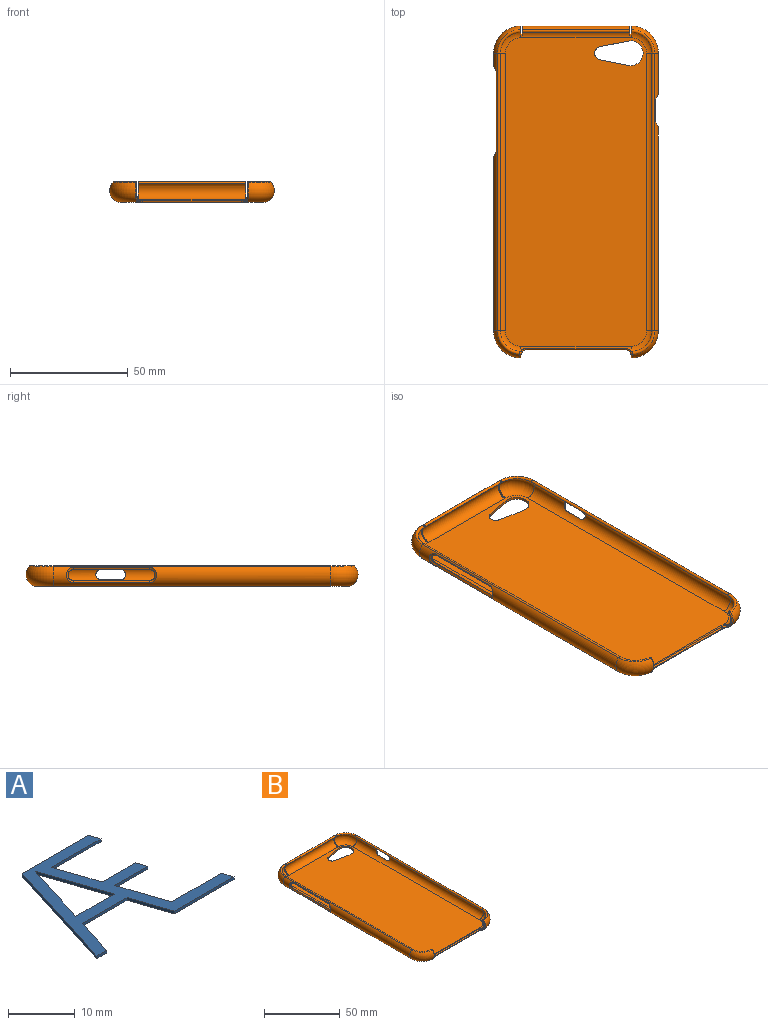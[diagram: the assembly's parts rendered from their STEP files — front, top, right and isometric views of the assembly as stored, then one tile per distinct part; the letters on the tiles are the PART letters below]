
ASSEMBLY  parts=2 mates=1
PART A: 21 faces, bbox 29x23x0.5 mm
  f0: plane 8x2.69mm, normal (0.95,0.32,0), area 4.2mm2, adj f1,f18,f19,f20
  f1: plane 10.46x0.5mm, normal (0,-1,0), area 5.2mm2, adj f0,f2,f19,f20
  f2: plane 2x0.67mm, normal (0.95,0.32,0), area 1.1mm2, adj f1,f3,f19,f20
  f3: plane 14.03x0.5mm, normal (0,1,0), area 7mm2, adj f2,f4,f19,f20
  f4: plane 23x7.2mm, normal (-0.95,0.3,0), area 12.1mm2, adj f3,f5,f19,f20
  f5: plane 2.1x0.5mm, normal (0,-1,0), area 1mm2, adj f4,f6,f19,f20
  f6: plane 7.49x2.35mm, normal (0.95,-0.3,0), area 3.9mm2, adj f5,f7,f19,f20
  f7: plane 9.44x0.5mm, normal (0,-1,0), area 4.7mm2, adj f6,f8,f19,f20
  f8: plane 7.49x2.52mm, normal (-0.95,-0.32,0), area 4mm2, adj f7,f9,f19,f20
  f9: plane 12.6x0.5mm, normal (0,-1,0), area 6.3mm2, adj f8,f10,f19,f20
  f10: plane 2x0.67mm, normal (0.95,0.32,0), area 1.1mm2, adj f9,f11,f19,f20
  f11: plane 10.48x0.5mm, normal (0,1,0), area 5.2mm2, adj f10,f12,f19,f20
  f12: plane 9x3.03mm, normal (0.95,0.32,0), area 4.7mm2, adj f11,f13,f19,f20
  f13: plane 7x0.5mm, normal (0,-1,0), area 3.5mm2, adj f12,f14,f19,f20
  f14: plane 2x0.67mm, normal (0.95,0.32,0), area 1.1mm2, adj f13,f18,f19,f20
  f15: plane 8.14x0.5mm, normal (0,1,0), area 4.1mm2, adj f16,f17,f19,f20
  f16: plane 12.53x3.92mm, normal (0.95,-0.3,0), area 6.6mm2, adj f15,f17,f19,f20
  f17: plane 12.53x4.22mm, normal (-0.95,-0.32,0), area 6.6mm2, adj f15,f16,f19,f20
  f18: plane 7x0.5mm, normal (0,1,0), area 3.5mm2, adj f0,f14,f19,f20
  f19: plane 29x23mm, normal (0,0,1), area 169.9mm2, adj f0,f1,f2,f3,f4,f5,f6,f7
  f20: plane 29x23mm, normal (0,0,-1), area 169.9mm2, adj f0,f1,f2,f3,f4,f5,f6,f7
PART B: 105 faces, bbox 71.8x143x9.1 mm
  f0: plane 131.13x59.96mm, normal (0,0,-1), area 7444.4mm2, adj f4,f6,f8,f14,f15,f16,f17,f18
  f1: cylinder r=0.7mm len=45.57mm, axis (-1,0,0), area 71.7mm2, adj f13,f18,f58,f60
  f2: plane 131.13x59.96mm, normal (0,0,1), area 7665.3mm2, adj f3,f5,f7,f9,f10,f11,f12,f13
  f3: cylinder r=3.88mm len=117.94mm, axis (0,1,0), area 1118.1mm2, adj f2,f10,f11,f30,f31,f32,f33,f38
  f4: cylinder r=4.98mm len=117.94mm, axis (0,1,0), area 1344mm2, adj f0,f14,f17,f38,f40,f41,f42,f43
  f5: cylinder r=3.88mm len=117.94mm, axis (0,1,0), area 982mm2, adj f2,f9,f12,f22,f23,f24,f25,f26
  f6: cylinder r=4.98mm len=117.94mm, axis (0,1,0), area 1133mm2, adj f0,f15,f16,f35,f44,f45,f46,f47
  f7: cylinder r=3.88mm len=46.77mm, axis (-1,0,0), area 43mm2, adj f2,f9,f10,f72,f74,f76
  f8: cylinder r=4.98mm len=46.77mm, axis (-1,0,0), area 53.5mm2, adj f0,f14,f15,f67,f69,f71
  f9: torus R=6.59mm, axis (0,0,-1), area 141.3mm2, adj f2,f5,f7,f34,f68,f70
  f10: torus R=6.59mm, axis (0,0,-1), area 141.3mm2, adj f2,f3,f7,f39,f78,f79
  f11: torus R=6.59mm, axis (0,0,-1), area 144.5mm2, adj f2,f3,f13,f37,f57
  f12: torus R=6.59mm, axis (0,0,-1), area 144.5mm2, adj f2,f5,f13,f36,f61
  f13: cylinder r=3.88mm len=46.77mm, axis (-1,0,0), area 448mm2, adj f1,f2,f11,f12,f58,f60,f101,f102
  f14: torus R=6.59mm, axis (0,0,-1), area 186.2mm2, adj f0,f4,f8,f39,f73,f75
  f15: torus R=6.59mm, axis (0,0,-1), area 186.2mm2, adj f0,f6,f8,f34,f64,f65
  f16: torus R=6.59mm, axis (0,0,-1), area 190.5mm2, adj f0,f6,f18,f36,f61
  f17: torus R=6.59mm, axis (0,0,-1), area 190.5mm2, adj f0,f4,f18,f37,f57
  f18: cylinder r=4.98mm len=46.77mm, axis (-1,0,0), area 543.2mm2, adj f0,f1,f16,f17,f58,f60,f103,f104
  f19: plane 41.97x0.14mm, normal (0,-1,0), area 6mm2, adj f62,f63,f69,f74
  f20: plane 5.67x1.68mm, normal (-1,0,0), area 0.9mm2, adj f62,f75,f77,f79
  f21: plane 5.67x1.68mm, normal (1,0,0), area 0.9mm2, adj f63,f64,f66,f68
  f22: plane 32.52x0.11mm, normal (0,0,-1), area 3.7mm2, adj f5,f23,f29,f47
  f23: cylinder r=2.2mm len=2.2mm, axis (1,0,0), area 1mm2, adj f5,f22,f24,f49
  f24: plane 0.47x0.15mm, normal (0,1,0), area 0.1mm2, adj f5,f23,f25,f51
  f25: cylinder r=2.2mm len=2.2mm, axis (1,0,0), area 1mm2, adj f5,f24,f26,f50
  f26: plane 32.52x0.06mm, normal (0,0,1), area 2.1mm2, adj f5,f25,f27,f48
  f27: cylinder r=2.2mm len=2.2mm, axis (1,0,0), area 1mm2, adj f5,f26,f28,f46
  f28: plane 0.47x0.15mm, normal (0,-1,0), area 0.1mm2, adj f5,f27,f29,f44
  f29: cylinder r=2.2mm len=2.2mm, axis (1,0,0), area 1mm2, adj f5,f22,f28,f45
  f30: cylinder r=2.24mm len=4.48mm, axis (-1,0,0), area 2.1mm2, adj f3,f31,f33,f42
  f31: plane 8.14x0.1mm, normal (0,0,1), area 0.8mm2, adj f3,f30,f32,f40
  f32: cylinder r=2.24mm len=4.48mm, axis (-1,0,0), area 2.1mm2, adj f3,f31,f33,f41
  f33: plane 8.14x0.1mm, normal (0,0,-1), area 0.8mm2, adj f3,f30,f32,f43
  f34: torus R=9.51mm, axis (0,0,1), area 22.3mm2, adj f9,f15,f35,f66,f68
  f35: cylinder r=0.7mm len=117.94mm, axis (0,1,0), area 185.6mm2, adj f5,f6,f34,f36
  f36: torus R=9.51mm, axis (0,0,1), area 23mm2, adj f12,f16,f35,f61
  f37: torus R=9.51mm, axis (0,0,1), area 23mm2, adj f11,f17,f38,f57
  f38: cylinder r=0.7mm len=117.94mm, axis (0,1,0), area 185.6mm2, adj f3,f4,f37,f39
  f39: torus R=9.51mm, axis (0,0,1), area 22.3mm2, adj f10,f14,f38,f77,f79
  f40: plane 8.14x1.05mm, normal (0.91,0,0.41), area 9.4mm2, adj f4,f31,f41,f42
  f41: bspline ~6.58x2.87mm, area 9mm2, adj f4,f32,f40,f43
  f42: bspline ~6.58x2.87mm, area 9mm2, adj f4,f30,f40,f43
  f43: plane 8.14x1.05mm, normal (0.91,0,-0.41), area 9.4mm2, adj f4,f33,f41,f42
  f44: cone r=4.34mm half-angle=45deg, axis (0,1,0), area 0.1mm2, adj f6,f28,f45,f46
  f45: bspline ~3.24x2.84mm, area 4.4mm2, adj f6,f29,f44,f47
  f46: bspline ~3.28x2.83mm, area 4.5mm2, adj f6,f27,f44,f48
  f47: plane 32.52x1.03mm, normal (-0.9,0,-0.43), area 37.2mm2, adj f6,f22,f45,f49
  f48: plane 32.52x1.08mm, normal (-0.92,0,0.39), area 37.9mm2, adj f6,f26,f46,f50
  f49: bspline ~3.25x2.83mm, area 4.4mm2, adj f6,f23,f47,f51
  f50: bspline ~3.28x2.83mm, area 4.5mm2, adj f6,f25,f48,f51
  f51: cone r=4.98mm half-angle=45deg, axis (0,-1,0), area 0.1mm2, adj f6,f24,f49,f50
  f52: plane 11.93x2.36mm, normal (0.19,0.98,0), area 13.4mm2, adj f0,f2,f53,f55
  f53: cylinder r=5.29mm len=10.57mm, axis (0,0,1), area 20.5mm2, adj f0,f2,f52,f54
  f54: plane 11.93x2.36mm, normal (0.19,-0.98,0), area 13.4mm2, adj f0,f2,f53,f55
  f55: cylinder r=2.88mm len=5.64mm, axis (0,0,1), area 8.7mm2, adj f0,f2,f52,f54
  f56: plane 0.6x0.1mm, normal (0,1,0), area 0.1mm2, adj f57,f58,f102,f104
  f57: plane 8.69x4.15mm, normal (-1,0,0), area 10.8mm2, adj f11,f17,f37,f56,f102,f104
  f58: plane 8.69x4.15mm, normal (1,0,0), area 10.8mm2, adj f1,f13,f18,f56,f102,f104
  f59: plane 0.6x0.1mm, normal (0,1,0), area 0.1mm2, adj f60,f61,f101,f103
  f60: plane 8.69x4.15mm, normal (-1,0,0), area 10.8mm2, adj f1,f13,f18,f59,f101,f103
  f61: plane 8.69x4.15mm, normal (1,0,0), area 10.8mm2, adj f12,f16,f36,f59,f101,f103
  f62: cylinder r=2.4mm len=2.4mm, axis (0,0,-1), area 0.6mm2, adj f19,f20,f71,f73,f76,f78
  f63: cylinder r=2.4mm len=2.4mm, axis (0,0,1), area 0.6mm2, adj f19,f21,f65,f67,f70,f72
  f64: bspline ~7.51x2.43mm, area 5.1mm2, adj f15,f21,f65,f66
  f65: bspline ~2.76x2.55mm, area 1.6mm2, adj f15,f63,f64,f67
  f66: bspline ~1.26x0.77mm, area 0.8mm2, adj f21,f34,f64,f68
  f67: bspline ~2.76x1.93mm, area 1.7mm2, adj f8,f63,f65,f69
  f68: bspline ~6.78x2.74mm, area 4.2mm2, adj f9,f21,f34,f66,f70
  f69: cylinder r=0.48mm len=41.97mm, axis (-1,0,0), area 27.3mm2, adj f8,f19,f67,f71
  f70: bspline ~2.88x2.4mm, area 1.7mm2, adj f9,f63,f68,f72
  f71: bspline ~3.23x1.93mm, area 1.7mm2, adj f8,f62,f69,f73
  f72: bspline ~3.22x1.94mm, area 2.2mm2, adj f7,f63,f70,f74
  f73: bspline ~2.76x2.55mm, area 1.6mm2, adj f14,f62,f71,f75
  f74: cylinder r=0.48mm len=41.97mm, axis (-1,0,0), area 36.1mm2, adj f7,f19,f72,f76
  f75: bspline ~7.51x2.43mm, area 5.1mm2, adj f14,f20,f73,f77
  f76: bspline ~3.22x1.94mm, area 2.2mm2, adj f7,f62,f74,f78
  f77: bspline ~1.26x0.77mm, area 0.8mm2, adj f20,f39,f75,f79
  f78: bspline ~2.39x2.33mm, area 1.7mm2, adj f10,f62,f76,f79
  f79: bspline ~6.71x2.89mm, area 4.2mm2, adj f10,f20,f39,f77,f78
  f80: plane 8x2.69mm, normal (0.95,-0.32,0), area 4.2mm2, adj f0,f81,f98,f99
  f81: plane 10.46x0.5mm, normal (0,1,0), area 5.2mm2, adj f0,f80,f82,f99
  f82: plane 2x0.67mm, normal (0.95,-0.32,0), area 1.1mm2, adj f0,f81,f83,f99
  f83: plane 14.03x0.5mm, normal (0,-1,0), area 7mm2, adj f0,f82,f84,f99
  f84: plane 23x7.2mm, normal (-0.95,-0.3,0), area 12.1mm2, adj f0,f83,f85,f99
  f85: plane 2.1x0.5mm, normal (0,1,0), area 1mm2, adj f0,f84,f86,f99
  f86: plane 7.49x2.35mm, normal (0.95,0.3,0), area 3.9mm2, adj f0,f85,f87,f99
  f87: plane 9.44x0.5mm, normal (0,1,0), area 4.7mm2, adj f0,f86,f88,f99
  f88: plane 7.49x2.52mm, normal (-0.95,0.32,0), area 4mm2, adj f0,f87,f89,f99
  f89: plane 12.6x0.5mm, normal (0,1,0), area 6.3mm2, adj f0,f88,f90,f99
  f90: plane 2x0.67mm, normal (0.95,-0.32,0), area 1.1mm2, adj f0,f89,f91,f99
  f91: plane 10.48x0.5mm, normal (0,-1,0), area 5.2mm2, adj f0,f90,f92,f99
  f92: plane 9x3.03mm, normal (0.95,-0.32,0), area 4.7mm2, adj f0,f91,f93,f99
  f93: plane 7x0.5mm, normal (0,1,0), area 3.5mm2, adj f0,f92,f94,f99
  f94: plane 2x0.67mm, normal (0.95,-0.32,0), area 1.1mm2, adj f0,f93,f98,f99
  f95: plane 8.14x0.5mm, normal (0,-1,0), area 4.1mm2, adj f96,f97,f99,f100
  f96: plane 12.53x3.92mm, normal (0.95,0.3,0), area 6.6mm2, adj f95,f97,f99,f100
  f97: plane 12.53x4.22mm, normal (-0.95,0.32,0), area 6.6mm2, adj f95,f96,f99,f100
  f98: plane 7x0.5mm, normal (0,-1,0), area 3.5mm2, adj f0,f80,f94,f99
  f99: plane 29x23mm, normal (0,0,-1), area 169.9mm2, adj f80,f81,f82,f83,f84,f85,f86,f87
  f100: plane 12.53x8.14mm, normal (0,0,-1), area 51mm2, adj f95,f96,f97
  f101: cylinder r=0.5mm len=0.61mm, axis (-1,0,0), area 0.5mm2, adj f13,f59,f60,f61
  f102: cylinder r=0.5mm len=0.61mm, axis (-1,0,0), area 0.5mm2, adj f13,f56,f57,f58
  f103: cylinder r=0.5mm len=0.6mm, axis (-1,0,0), area 0.4mm2, adj f18,f59,f60,f61
  f104: cylinder r=0.5mm len=0.6mm, axis (-1,0,0), area 0.4mm2, adj f18,f56,f57,f58
PLACE A rot(axis=(0,1,0),180deg) t=(-93.96,-46.88,-20.05)mm
PLACE B t=(-107.46,-5.92,-15.57)mm
MATE fastened A.f20 <-> B.f99  axis (0,0,1) through (-101.17,-23.88,-20.05)mm
